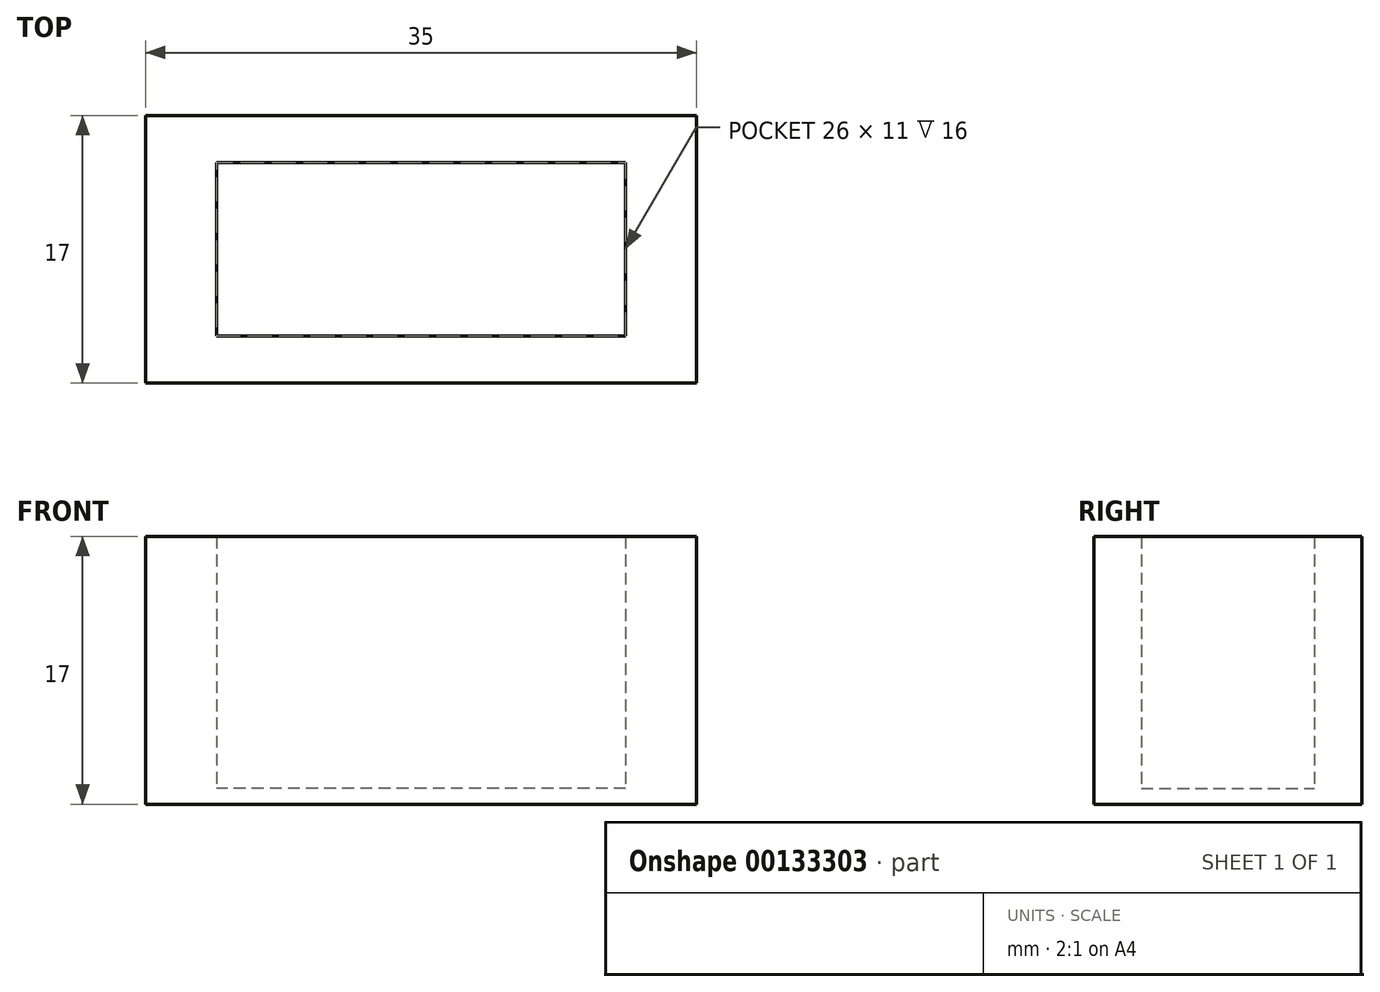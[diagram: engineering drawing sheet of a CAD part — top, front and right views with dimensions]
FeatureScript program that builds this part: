
annotation { "Feature Type Name" : "Feature", "Feature Type Description" : "" }
export const myFeature = defineFeature(function(context is Context, id is Id, definition is map)
    precondition{}
    {
        {
            var Q0;
            Q0=qCreatedBy(makeId("Top.planeOp"),FACE);
            var sketch = newSketch(context, id + "F0", { "sketchPlane" : qUnion([Q0])});
            skLineSegment(sketch, "E0.bottom", {"start": v(17.5, -8.5) * mm, "end": v(-17.5, -8.5) * mm});
            skLineSegment(sketch, "E0.top", {"start": v(17.5, 8.5) * mm, "end": v(-17.5, 8.5) * mm});
            skLineSegment(sketch, "E0.left", {"start": v(17.5, -8.5) * mm, "end": v(17.5, 8.5) * mm});
            skLineSegment(sketch, "E0.right", {"start": v(-17.5, -8.5) * mm, "end": v(-17.5, 8.5) * mm});
            skPoint(sketch, "E0.middle", {"position": v(0, 0) * mm});
            skLineSegment(sketch, "E1.bottom", {"start": v(13, -5.5) * mm, "end": v(-13, -5.5) * mm});
            skLineSegment(sketch, "E1.top", {"start": v(13, 5.5) * mm, "end": v(-13, 5.5) * mm});
            skLineSegment(sketch, "E1.left", {"start": v(13, -5.5) * mm, "end": v(13, 5.5) * mm});
            skLineSegment(sketch, "E1.right", {"start": v(-13, -5.5) * mm, "end": v(-13, 5.5) * mm});
            skSolve(sketch);
        }
        {
            var Q0;
            Q0=makeQuery(id+"F0.imprint","IMPRINT",FACE,{"disambiguationData":[TD([[makeQuery(id+"F0.imprint","IMPRINT",EDGE,{"derivedFrom":sQuery(id+"F0.wireOp",EDGE,"E1.bottom")}),-1.0]])]});
            extrude(context, id + "F1", {"entities" : qUnion([Q0]), "depth" : 1 * mm});
        }
        {
            var Q0;
            Q0=makeQuery(id+"F0.imprint","IMPRINT",FACE,{"disambiguationData":[TD([[makeQuery(id+"F0.imprint","IMPRINT",EDGE,{"derivedFrom":sQuery(id+"F0.wireOp",EDGE,"E0.bottom")}),-1.0]])]});
            extrude(context, id + "F2", {"entities" : qUnion([Q0]), "operationType" : NewBodyOperationType.ADD, "depth" : 17 * mm});
        }
    });
